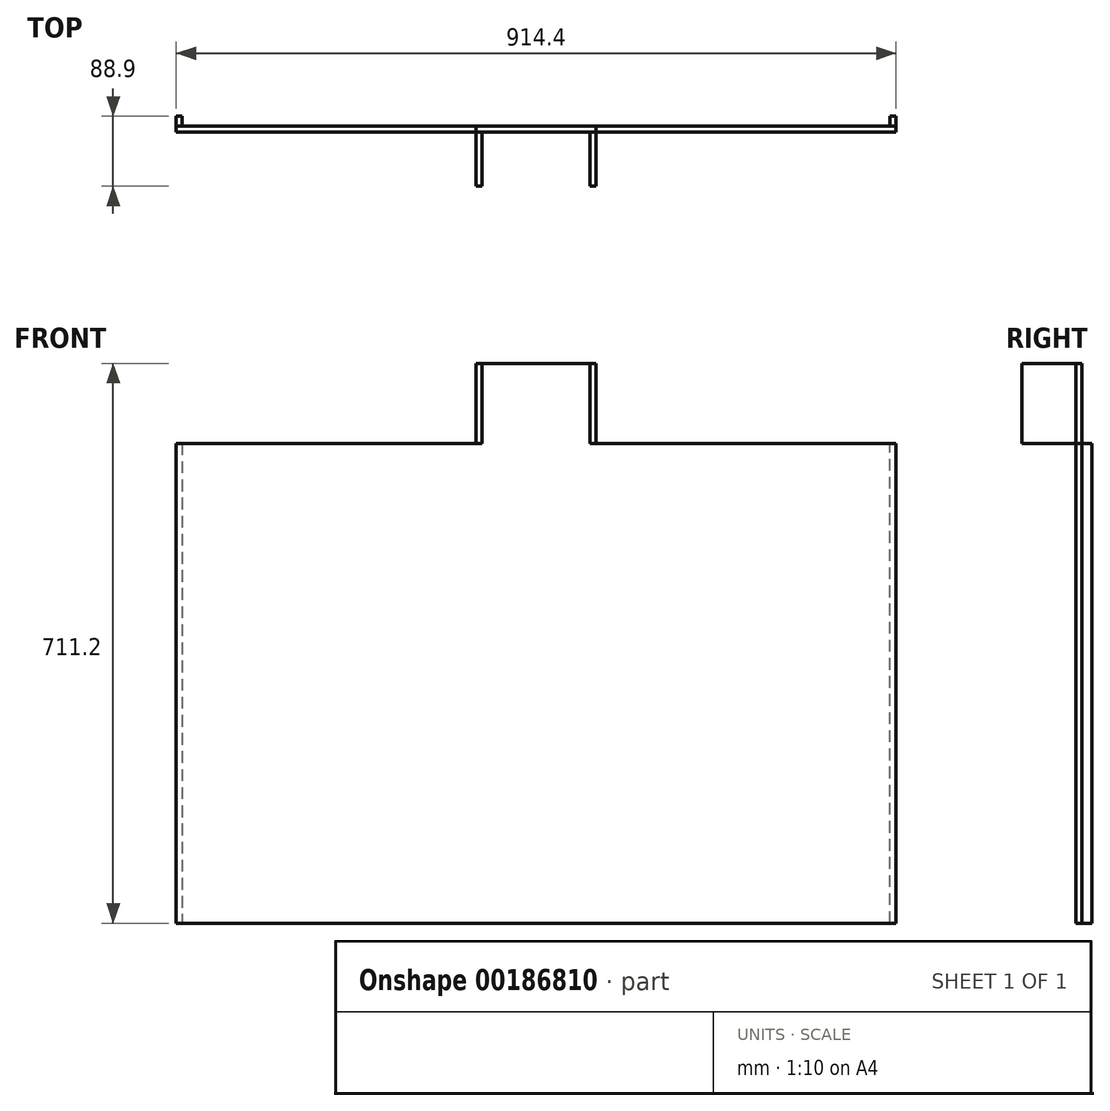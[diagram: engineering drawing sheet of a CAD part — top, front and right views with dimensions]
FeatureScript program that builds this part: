
annotation { "Feature Type Name" : "Feature", "Feature Type Description" : "" }
export const myFeature = defineFeature(function(context is Context, id is Id, definition is map)
    precondition{}
    {
        {
            var Q0;
            Q0=qCreatedBy(makeId("Front.planeOp"),FACE);
            var sketch = newSketch(context, id + "F0", { "sketchPlane" : qUnion([Q0])});
            skLineSegment(sketch, "E0", {"start": v(0, 0) * mm, "end": v(914.4, 0) * mm});
            skLineSegment(sketch, "E1", {"start": v(914.4, 0) * mm, "end": v(914.4, 609.6) * mm});
            skLineSegment(sketch, "E2", {"start": v(0, 609.6) * mm, "end": v(0, 0) * mm});
            skLineSegment(sketch, "E3", {"start": v(914.4, 609.6) * mm, "end": v(533.4, 609.6) * mm});
            skLineSegment(sketch, "E4", {"start": v(533.4, 609.6) * mm, "end": v(533.4, 711.2) * mm});
            skLineSegment(sketch, "E5", {"start": v(533.4, 711.2) * mm, "end": v(381, 711.2) * mm});
            skLineSegment(sketch, "E6", {"start": v(381, 711.2) * mm, "end": v(381, 609.6) * mm});
            skLineSegment(sketch, "E7", {"start": v(381, 609.6) * mm, "end": v(0, 609.6) * mm});
            skSolve(sketch);
        }
        {
            var Q0;
            Q0=makeQuery(id+"F0.imprint","IMPRINT",FACE,{"disambiguationData":[TD([[makeQuery(id+"F0.imprint","IMPRINT",EDGE,{"derivedFrom":sQuery(id+"F0.wireOp",EDGE,"E0")}),1.0]])]});
            extrude(context, id + "F1", {"entities" : qUnion([Q0]), "depth" : 7.62 * mm});
        }
        {
            var Q0;
            Q0=makeQuery(id+"F1.opExtrude","SWEPT_FACE",FACE,{"disambiguationData":[OSD([sQuery(id+"F0.wireOp",EDGE,"E6")])]});
            var sketch = newSketch(context, id + "F2", { "sketchPlane" : qUnion([Q0])});
            skLineSegment(sketch, "E8.bottom", {"start": v(0, 609.6) * mm, "end": v(76.2, 609.6) * mm});
            skLineSegment(sketch, "E8.top", {"start": v(0, 711.2) * mm, "end": v(76.2, 711.2) * mm});
            skLineSegment(sketch, "E8.left", {"start": v(0, 609.6) * mm, "end": v(0, 711.2) * mm});
            skLineSegment(sketch, "E8.right", {"start": v(76.2, 609.6) * mm, "end": v(76.2, 711.2) * mm});
            skSolve(sketch);
        }
        {
            var Q0;
            {var subQ2=sQuery(id+"F2.wireOp",EDGE,"E8.right");Q0=makeQuery(id+"F2.imprint","IMPRINT",FACE,{"disambiguationData":[TD([[makeQuery(id+"F2.imprint","IMPRINT",EDGE,{"derivedFrom":subQ2}),1.0]])]});}
            extrude(context, id + "F3", {"entities" : qUnion([Q0]), "oppositeDirection" : true, "depth" : 7.62 * mm});
        }
        {
            var Q0;
            Q0=makeQuery(id+"F1.opExtrude","SWEPT_FACE",FACE,{"disambiguationData":[OSD([sQuery(id+"F0.wireOp",EDGE,"E4")])]});
            var sketch = newSketch(context, id + "F4", { "sketchPlane" : qUnion([Q0])});
            skLineSegment(sketch, "E9.bottom", {"start": v(0, 609.6) * mm, "end": v(-76.2, 609.6) * mm});
            skLineSegment(sketch, "E9.top", {"start": v(0, 711.2) * mm, "end": v(-76.2, 711.2) * mm});
            skLineSegment(sketch, "E9.left", {"start": v(0, 609.6) * mm, "end": v(0, 711.2) * mm});
            skLineSegment(sketch, "E9.right", {"start": v(-76.2, 609.6) * mm, "end": v(-76.2, 711.2) * mm});
            skSolve(sketch);
        }
        {
            var Q0;
            {var subQ2=sQuery(id+"F4.wireOp",EDGE,"E9.right");Q0=makeQuery(id+"F4.imprint","IMPRINT",FACE,{"disambiguationData":[TD([[makeQuery(id+"F4.imprint","IMPRINT",EDGE,{"derivedFrom":subQ2}),-1.0]])]});}
            extrude(context, id + "F5", {"entities" : qUnion([Q0]), "oppositeDirection" : true, "depth" : 7.62 * mm});
        }
        {
            var Q0;
            Q0=makeQuery(id+"F1.opExtrude","SWEPT_FACE",FACE,{"disambiguationData":[OSD([sQuery(id+"F0.wireOp",EDGE,"E1")])]});
            var sketch = newSketch(context, id + "F6", { "sketchPlane" : qUnion([Q0])});
            skLineSegment(sketch, "E10.bottom", {"start": v(12.7, 0) * mm, "end": v(0, 0) * mm});
            skLineSegment(sketch, "E10.top", {"start": v(12.7, 609.6) * mm, "end": v(0, 609.6) * mm});
            skLineSegment(sketch, "E10.left", {"start": v(0, 0) * mm, "end": v(0, 609.6) * mm});
            skLineSegment(sketch, "E10.right", {"start": v(12.7, 0) * mm, "end": v(12.7, 609.6) * mm});
            skSolve(sketch);
        }
        {
            var Q0;
            Q0=makeQuery(id+"F6.imprint","IMPRINT",FACE,{"disambiguationData":[TD([[makeQuery(id+"F6.imprint","IMPRINT",EDGE,{"derivedFrom":sQuery(id+"F6.wireOp",EDGE,"E10.bottom")}),-1.0]])]});
            extrude(context, id + "F7", {"entities" : qUnion([Q0]), "oppositeDirection" : true, "depth" : 7.62 * mm});
        }
        {
            var Q0;
            Q0=makeQuery(id+"F1.opExtrude","SWEPT_FACE",FACE,{"disambiguationData":[OSD([sQuery(id+"F0.wireOp",EDGE,"E2")])]});
            var sketch = newSketch(context, id + "F8", { "sketchPlane" : qUnion([Q0])});
            skLineSegment(sketch, "E11.bottom", {"start": v(0, 0) * mm, "end": v(-12.7, 0) * mm});
            skLineSegment(sketch, "E11.top", {"start": v(0, 609.6) * mm, "end": v(-12.7, 609.6) * mm});
            skLineSegment(sketch, "E11.left", {"start": v(0, 0) * mm, "end": v(0, 609.6) * mm});
            skLineSegment(sketch, "E11.right", {"start": v(-12.7, 0) * mm, "end": v(-12.7, 609.6) * mm});
            skSolve(sketch);
        }
        {
            var Q0;
            Q0=makeQuery(id+"F8.imprint","IMPRINT",FACE,{"disambiguationData":[TD([[makeQuery(id+"F8.imprint","IMPRINT",EDGE,{"derivedFrom":sQuery(id+"F8.wireOp",EDGE,"E11.bottom")}),-1.0]])]});
            extrude(context, id + "F9", {"entities" : qUnion([Q0]), "oppositeDirection" : true, "depth" : 7.62 * mm});
        }
    });
